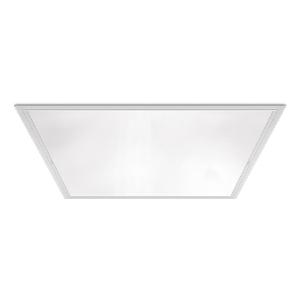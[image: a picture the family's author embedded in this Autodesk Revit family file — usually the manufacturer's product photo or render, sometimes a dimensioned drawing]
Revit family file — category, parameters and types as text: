
# Revit family: 3f_filippi_-_l_340_luce_diffusa_lgs_ip65v_3f_filippi_-_23973_-_l_340_38w-840_lgs_ip65v_596x596
name_source: partatom
category: Lighting Fixtures
units: mm (PartAtom-declared; Revit-internal decimal feet)

## family parameters
Cut with Voids When Loaded = No
Host = Face
Light Source = No
Part Type = Normal
Room Calculation Point = No
Round Connector Dimension = Use Diameter
Shared = No

## types (1)
- 3F Filippi - L 340 Luce Diffusa LGS IP65V (1 x LED, 5677 lm, 45 W, 4000 K)
    Apparent Load = 45 VA
    Approval mark = ENEC
    CIE Flux Codes = 67 92 98 100 100
    Color Rendering = 80
    Color Temperature = 4000 K
    Control Gear = Electronic ballast
    Default Elevation = 1800 mm
    Description = ILLUMINOTECHNICAL
Luminous efficiency 100% (DLOR 100%, ULOR 0%).
Initial luminous flux of the luminaire 5677 lm.
Direct symmetric distribution.
Installation Interdistance Transv.D = 1.19 x hu - Long.D = 1.17 x hu.
Average luminance <3000 cd/m² for radial angles >65°.
Tabular UGR (CIE 117 - 4H-8H; S=0.25H; 70/50/20): RUG 17.8 - 17.8.
Beam angle: 87° - 86°.
Luminous efficacy 126 lm/W.
Lifetime (L93/B10): 30000 h. (tq+25°C)
Lifetime (L90/B10): 50000 h. (tq+25°C)
Lifetime (L85/B10): 80000 h. (tq+25°C)
Lifetime (L80/B10): 100000 h. (tq+25°C)
Sudden decreased luminous flux after 50000 hours: 0% (C0).
Photobiological safety in compliance with IEC/TR 62778: RG0 risk exempt, (IEC 62471).
In compliance with IEC/EN 62722-2-1 - IEC/EN 62717 standards.

SOURCE
Squared LED module 38W/840.
Energy efficiency class (UE 2019/2020 - UE 2019/2015): C.
CIE 13.3 Colour rendering index: CRI >80 (R9 <50%).
IES TM-30 Fidelity Index: Rf = 84 Rg = 95.
CCT nominal colour temperature 4000 K.
Colour initial tolerance (MacAdam): SDCM 3.

MECHANICAL
Housing in hot-galvanised steel, painted in white polyester.
Perimetral frame in white polycarbonate.
LGS micro-prismatic flat diffuser in transparent methacrylate (PMMA), multi-lenticular exterior, anti-glare.
Anti-glare opal polycarbonate filter for brightness uniformity.
Luminaire with limited surface temperature. - D - (EN 60598-2-24)
Dimensions: 596x596 mm, height 80 mm. Weight 4.45 kg.
IP65 protection degree for exposed part, IP40 for recessed part.
Mechanical strength to impacts IK06 (1 joule).
Glow-wire test resistance 650°C.

ELECTRICAL
Wiring on a separate unit.
Halogen Free electronic wiring 230V-50/60Hz, power factor 0.95, THD <25%, constant output current, SELV, class II, 1 driver.
Power of the luminaire 45 W.
CE - IEC 60598-1 - EN 60598-1.
SAFE FLICKER: PstLM=<1 and SVM=<0.4 (IEC TR 61547-1 and IEC TR 63158), to ensure a more comfortable and safe light.
Luminaire compliant with EN 60598-2-22 for power supply from a centralised emergency system CPSS (Central Power Supply System), not incorporated in the luminaire - high risk areas excluded. The default power and flux are 100% in AC and 100% in DC.
Ambient temperature from 0°C to +40°C.
Temperature class T6 max 85°C.
Relative humidity UR: <85%.

INSTALLATION
Lay-on or pull-up recessed fitting using frame accessory.
All accessories dedicated to this product are available on the Catalog and on our website www.3F-Filippi.com.

APPLICATIONS
Suitable product for food production plants (HACCP), IFS (Food Version 6), BRC (GSFS Food Version 7).
In environments requiring protection and simplified cleaning.
Hospitals, pharmaceutical, chemical, aseptic laboratories, sterilised rooms.
Environments: with VDTs, meeting rooms, offices.
Environments: architectural, commercial, staterooms, banks.
Environments where demanding visual tasks are performed and soft diffuse light is required for optimal visual comfort and total shielding of the light source.

WARNING
Luminaire designed for disposal/recycling at end-of-life.
Replaceable (LED only) light source by a professional. Replaceable control gear by a professional.
    Height = 0 mm  [stored 0 ft]
    Lamp = 1 x LED
    Lamp Light Flux = 5677 lm
    Lamp Power = 45 W
    Lamp count = 1
    Length = 596 mm
    Lifetime = 50000 h
    Luminous efficacy = 126 lm/W
    Manufacturer = 3F Filippi
    ModVariant = No
    Model = 3F Filippi - 23973 - L 340 38W-840 LGS IP65V 596x596
    Mounting Place = Ceiling
    Mounting Type = Recessed
    Number of Poles = 1
    OnlyDefault = Yes
    Power Factor = 1
    Product Name = 3F Filippi - L 340 Luce Diffusa LGS IP65V
    Product group = recessed luminaire
    ProductGroupID = 4
    Protection Class = Protection class II
    Protection Degree = IP 40
    RLX_Detail_Level = 1
    RLX_Emergency_Light_Flux = 0 lm
    RLX_Emergency_Type = 0
    RLX_Emergency_Type_DB = No
    RlxData = <blob elided: 154093 chars, md5=d9a75321>
    Socket = socket
    Standby Power = 0 W
    System Light Flux = 5677 lm
    System Power = 45 W
    Type Comments = Product without accessories
    Type Image = 3ffilippi_l_340_luce_diffusa_lgs_ip65v.jpg
    URL = http://relux.com
    VarID = ---
    Voltage = 0 V
    Weight = 0.00 kg
    Width = 596 mm

note: [stored X ft] marks values corroborated as IEEE doubles in the binary element streams (Revit-internal decimal feet)

## geometry (parser evidence)
native form markers: Blend x4, Sweep x10
no freeform markers — native parametric forms only
